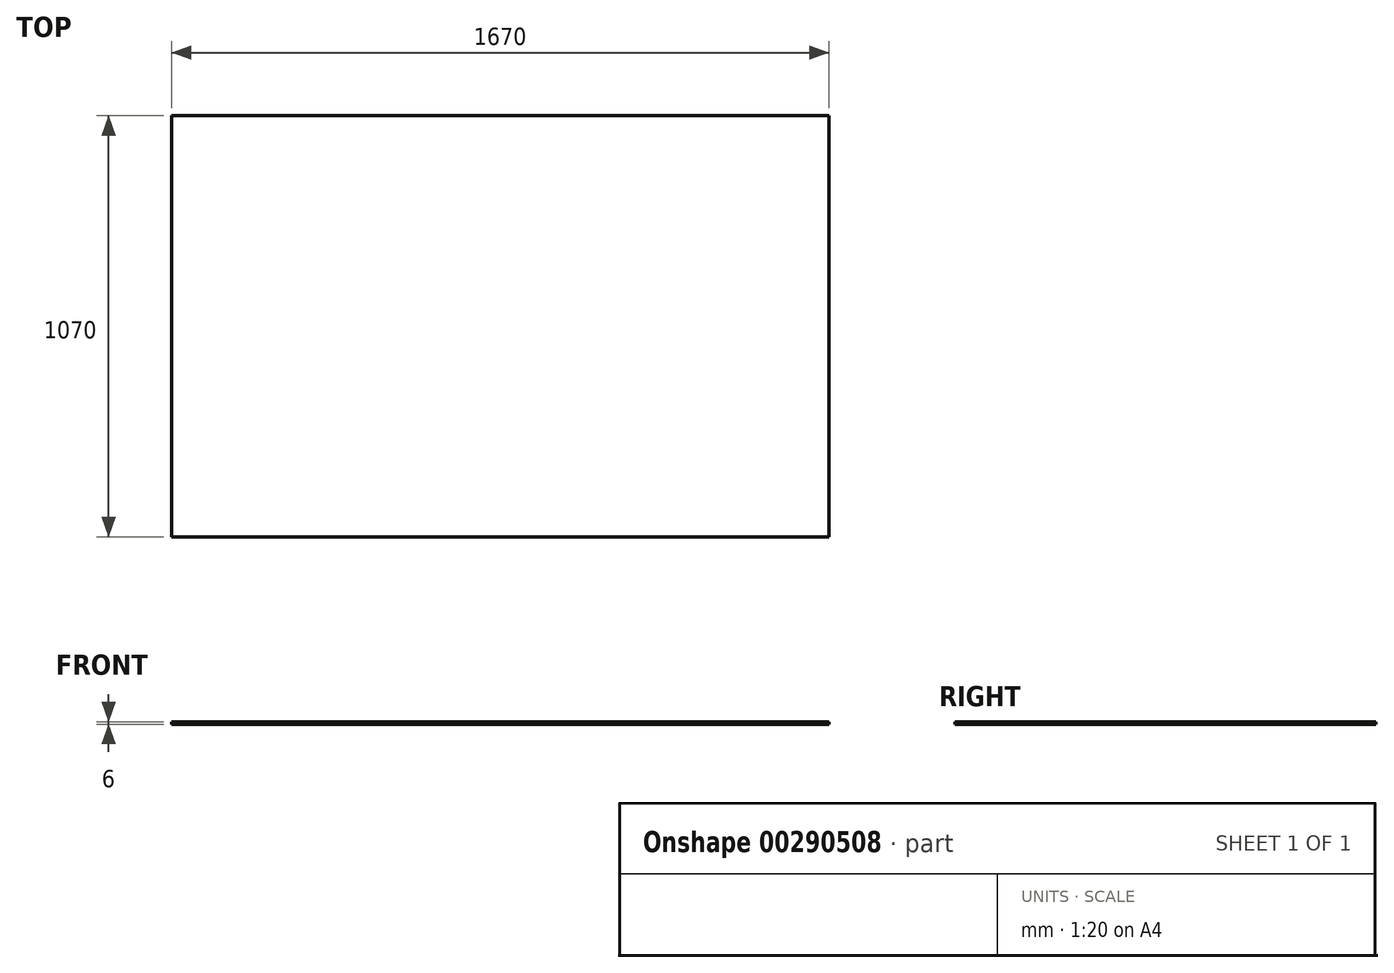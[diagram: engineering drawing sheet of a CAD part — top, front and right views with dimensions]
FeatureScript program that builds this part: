
annotation { "Feature Type Name" : "Feature", "Feature Type Description" : "" }
export const myFeature = defineFeature(function(context is Context, id is Id, definition is map)
    precondition{}
    {
        {
            var Q0;
            Q0=qCreatedBy(makeId("Top.planeOp"),FACE);
            var sketch = newSketch(context, id + "F0", { "sketchPlane" : qUnion([Q0])});
            skLineSegment(sketch, "E0.bottom", {"start": v(835, 535) * mm, "end": v(-835, 535) * mm});
            skLineSegment(sketch, "E0.top", {"start": v(835, -535) * mm, "end": v(-835, -535) * mm});
            skLineSegment(sketch, "E0.left", {"start": v(835, 535) * mm, "end": v(835, -535) * mm});
            skLineSegment(sketch, "E0.right", {"start": v(-835, 535) * mm, "end": v(-835, -535) * mm});
            skPoint(sketch, "E0.middle", {"position": v(0, 0) * mm});
            skSolve(sketch);
        }
        {
            var Q0;
            Q0 = qSketchRegion(id + "F0", true);
            extrude(context, id + "F1", {"entities" : qUnion([Q0]), "oppositeDirection" : true, "depth" : 6 * mm});
        }
    });
